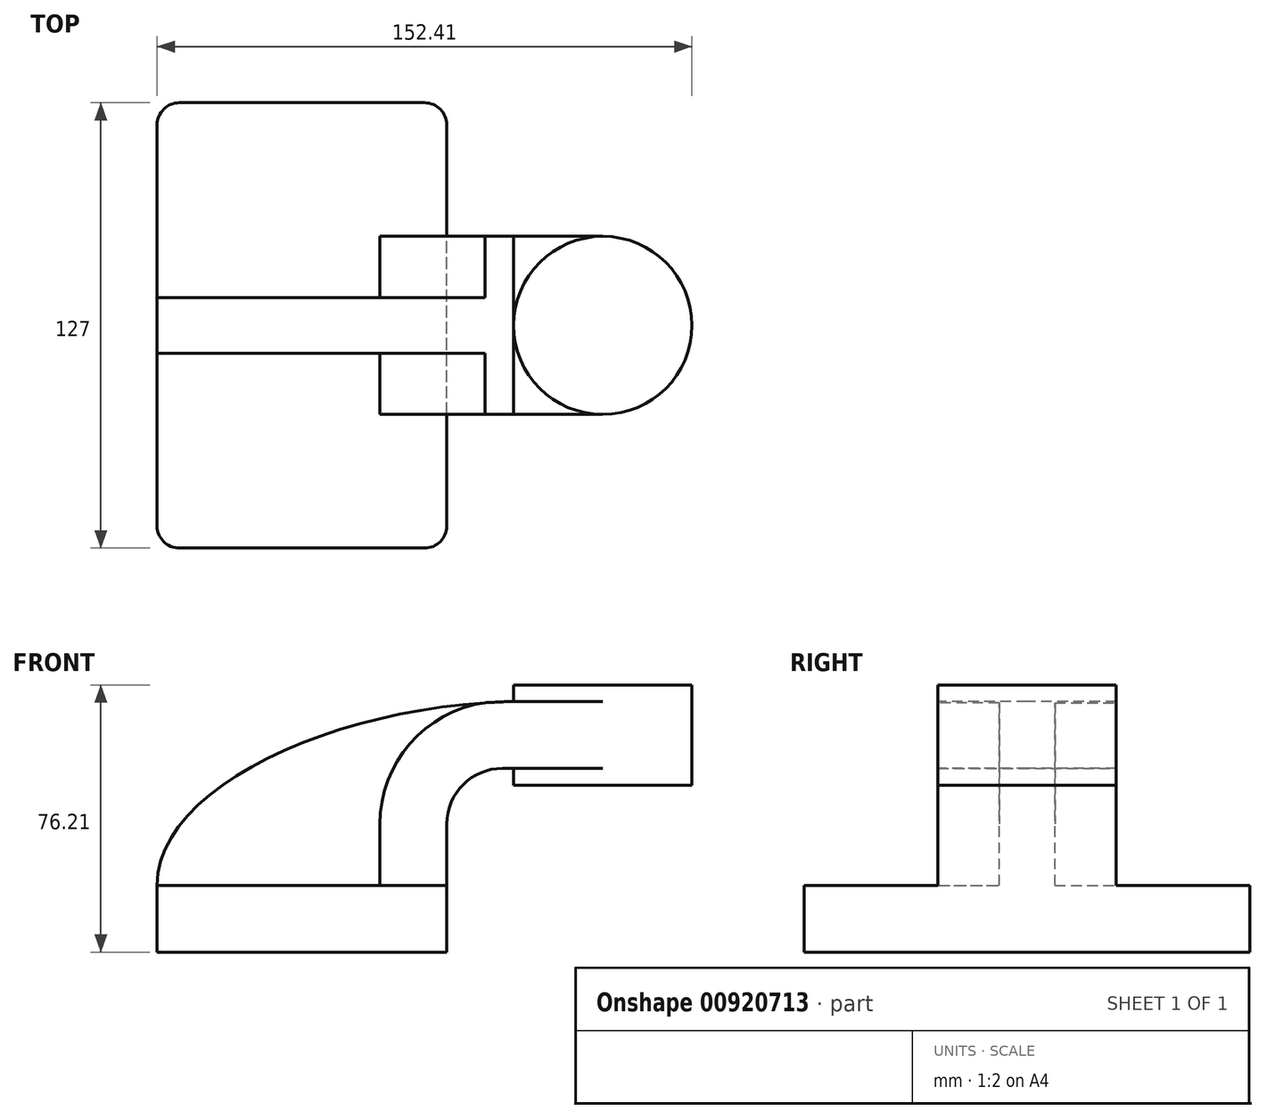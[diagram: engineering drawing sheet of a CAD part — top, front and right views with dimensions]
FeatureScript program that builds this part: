
annotation { "Feature Type Name" : "Feature", "Feature Type Description" : "" }
export const myFeature = defineFeature(function(context is Context, id is Id, definition is map)
    precondition{}
    {
        {
            var Q0;
            Q0=qCreatedBy(makeId("Front.planeOp"),FACE);
            var sketch = newSketch(context, id + "F0", { "sketchPlane" : qUnion([Q0])});
            skLineSegment(sketch, "E0.bottom", {"start": v(-41.28, -9.52) * mm, "end": v(41.27, -9.52) * mm});
            skLineSegment(sketch, "E0.top", {"start": v(-41.28, 9.53) * mm, "end": v(41.27, 9.53) * mm});
            skLineSegment(sketch, "E0.left", {"start": v(-41.28, -9.52) * mm, "end": v(-41.28, 9.53) * mm});
            skLineSegment(sketch, "E0.right", {"start": v(41.27, -9.52) * mm, "end": v(41.27, 9.53) * mm});
            skPoint(sketch, "E0.middle", {"position": v(0, 0) * mm});
            skLineSegment(sketch, "E1.bottom", {"start": v(60.32, 38.1) * mm, "end": v(111.12, 38.1) * mm});
            skLineSegment(sketch, "E1.top", {"start": v(60.32, 66.68) * mm, "end": v(111.12, 66.68) * mm});
            skLineSegment(sketch, "E1.left", {"start": v(60.32, 38.1) * mm, "end": v(60.32, 66.68) * mm});
            skLineSegment(sketch, "E1.right", {"start": v(111.12, 38.1) * mm, "end": v(111.12, 66.68) * mm});
            skPoint(sketch, "E1.middle", {"position": v(85.72, 52.39) * mm});
            skLineSegment(sketch, "E2", {"start": v(41.27, 9.53) * mm, "end": v(41.27, 27) * mm});
            skArc(sketch, "E3", {"start": v(41.27, 27) * mm, "mid": v(45.92, 38.23) * mm, "end": v(57.15, 42.88) * mm});
            skLineSegment(sketch, "E4", {"start": v(57.15, 42.88) * mm, "end": v(85.72, 42.88) * mm});
            skLineSegment(sketch, "E5.0", {"start": v(57.15, 61.93) * mm, "end": v(85.72, 61.93) * mm});
            skArc(sketch, "E5.1", {"start": v(22.22, 27) * mm, "mid": v(32.45, 51.7) * mm, "end": v(57.15, 61.93) * mm});
            skLineSegment(sketch, "E5.2", {"start": v(22.22, 9.53) * mm, "end": v(22.22, 27) * mm});
            skLineSegment(sketch, "E6", {"start": v(85.72, 38.1) * mm, "end": v(85.72, 66.68) * mm});
            skFitSpline(sketch, "E7", {"points": [v(-41.28, 9.53) * mm, v(60.32, 61.93) * mm], "startDerivative": vector(0.16, 85.8) * mm, "endDerivative": vector(149.42, 2.97) * mm});
            skSolve(sketch);
        }
        {
            var Q0;
            Q0=makeQuery(id+"F0.imprint","IMPRINT",FACE,{"disambiguationData":[TD([[makeQuery(id+"F0.imprint","IMPRINT",EDGE,{"derivedFrom":sQuery(id+"F0.wireOp",EDGE,"E0.bottom")}),1.0]])]});
            extrude(context, id + "F1", {"entities" : qUnion([Q0]), "endBound" : BoundingType.SYMMETRIC, "depth" : 127 * mm, "offsetDistance" : 25.4 * mm});
        }
        {
            var Q0;
            {var subQ1=sQuery(id+"F0.wireOp",EDGE,"E2");Q0=makeQuery(id+"F0.imprint","IMPRINT",FACE,{"disambiguationData":[TD([[makeQuery(id+"F0.imprint","IMPRINT",EDGE,{"derivedFrom":subQ1}),1.0]])]});}
            extrude(context, id + "F2", {"entities" : qUnion([Q0]), "operationType" : NewBodyOperationType.ADD, "endBound" : BoundingType.SYMMETRIC, "depth" : 50.8 * mm, "offsetDistance" : 25.4 * mm});
        }
        {
            var Q0;
            {var subQ3=sQuery(id+"F0.wireOp",EDGE,"E5.2");Q0=makeQuery(id+"F0.imprint","IMPRINT",FACE,{"disambiguationData":[TD([[makeQuery(id+"F0.imprint","IMPRINT",EDGE,{"derivedFrom":subQ3}),1.0]])]});}
            extrude(context, id + "F3", {"entities" : qUnion([Q0]), "operationType" : NewBodyOperationType.ADD, "endBound" : BoundingType.SYMMETRIC, "depth" : 15.88 * mm, "offsetDistance" : 25.4 * mm});
        }
        {
            var Q0;
            {var subQ3=sQuery(id+"F0.wireOp",EDGE,"E4");var subQ5=sQuery(id+"F0.wireOp",EDGE,"E6");var subQ6=makeQuery(id+"F0.imprint","INTERSECT",VERTEX,{"derivedFrom":[subQ3,subQ5]});Q0=makeQuery(id+"F0.imprint","IMPRINT",FACE,{"disambiguationData":[TD([[makeQuery(id+"F0.imprint","IMPRINT",EDGE,{"disambiguationData":[TD([[subQ6,1.0]])],"derivedFrom":subQ3}),1.0]])]});}
            extrude(context, id + "F4", {"entities" : qUnion([Q0]), "operationType" : NewBodyOperationType.ADD, "endBound" : BoundingType.SYMMETRIC, "depth" : 50.8 * mm, "offsetDistance" : 25.4 * mm});
        }
        {
            var Q0;
            {var subQ4=sQuery(id+"F0.wireOp",EDGE,"E1.right");Q0=makeQuery(id+"F0.imprint","IMPRINT",FACE,{"disambiguationData":[TD([[makeQuery(id+"F0.imprint","IMPRINT",EDGE,{"derivedFrom":subQ4}),1.0]])]});}
            var Q1;
            Q1=sQuery(id+"F0.wireOp",EDGE,"E6");
            revolve(context, id + "F5", {"operationType" : NewBodyOperationType.ADD, "surfaceOperationType" : NewSurfaceOperationType.NEW, "entities" : qUnion([Q0]), "axis" : qUnion([Q1]), "revolveType" : RevolveType.FULL});
        }
        {
            var Q0;
            Q0=makeQuery(id+"F1.opExtrude","CAP_EDGE",EDGE,{"disambiguationData":[OSD([sQuery(id+"F0.wireOp",EDGE,"E0.right")])],"isStart":false});
            var Q1;
            Q1=makeQuery(id+"F1.opExtrude","CAP_EDGE",EDGE,{"disambiguationData":[OSD([sQuery(id+"F0.wireOp",EDGE,"E0.left")])],"isStart":false});
            var Q2;
            Q2=makeQuery(id+"F1.opExtrude","CAP_EDGE",EDGE,{"disambiguationData":[OSD([sQuery(id+"F0.wireOp",EDGE,"E0.right")])],"isStart":true});
            var Q3;
            Q3=makeQuery(id+"F1.opExtrude","CAP_EDGE",EDGE,{"disambiguationData":[OSD([sQuery(id+"F0.wireOp",EDGE,"E0.left")])],"isStart":true});
            fillet(context, id + "F6", {"entities" : qUnion([Q0, Q1, Q2, Q3]), "radius" : 6.35 * mm, "tangentPropagation" : true, "allowEdgeOverflow" : false});
        }
    });
